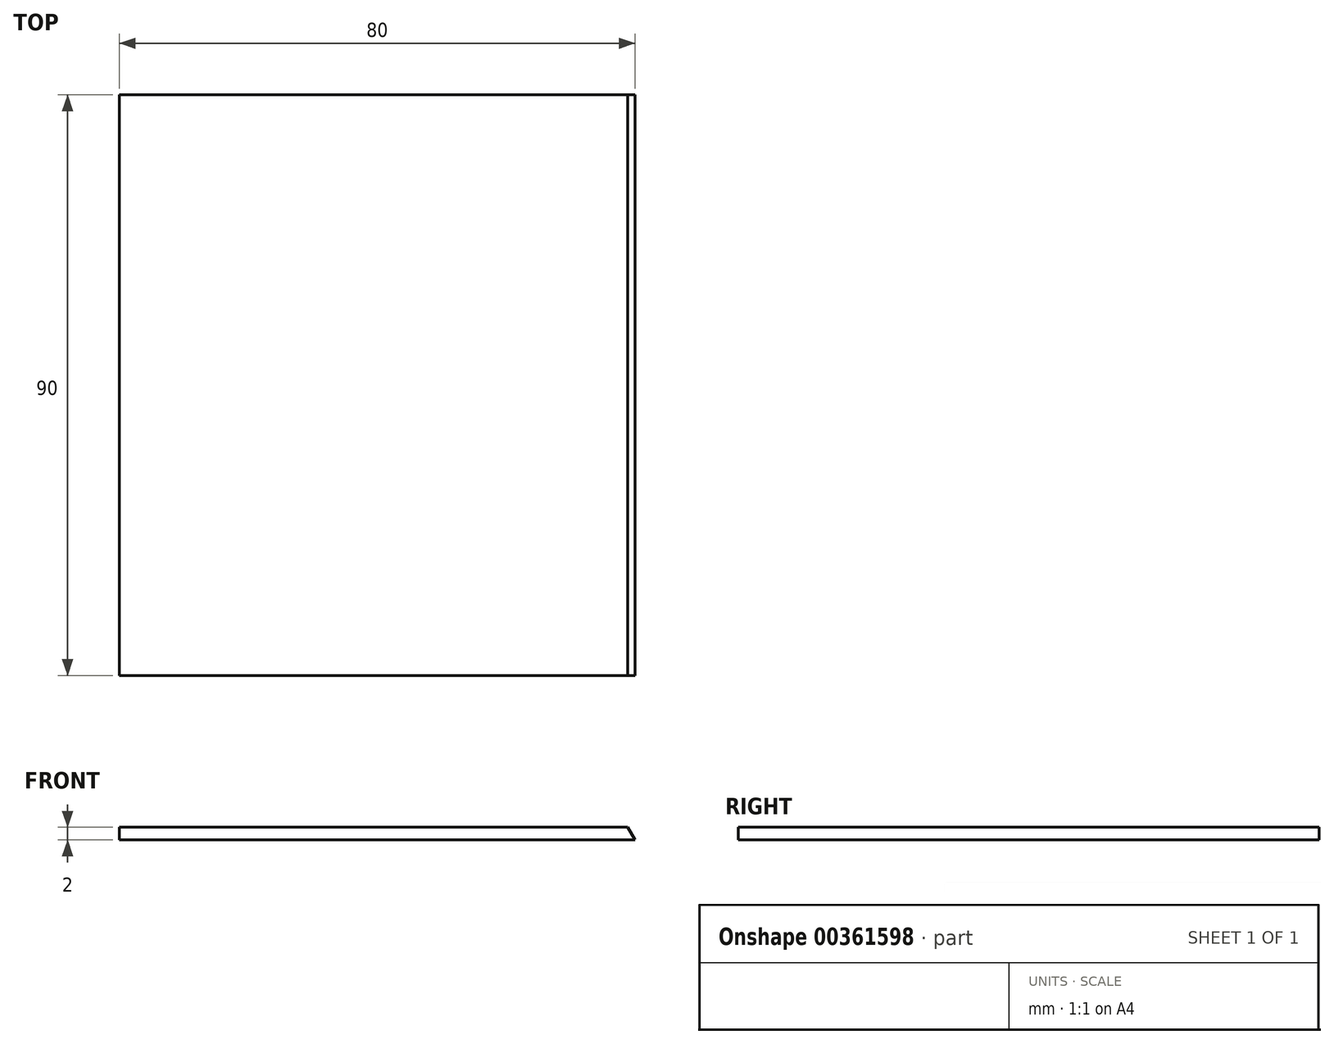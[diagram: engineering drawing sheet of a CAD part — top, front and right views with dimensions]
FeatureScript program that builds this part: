
annotation { "Feature Type Name" : "Feature", "Feature Type Description" : "" }
export const myFeature = defineFeature(function(context is Context, id is Id, definition is map)
    precondition{}
    {
        {
            var Q0;
            Q0=qCreatedBy(makeId("Front.planeOp"),FACE);
            var sketch = newSketch(context, id + "F0", { "sketchPlane" : qUnion([Q0])});
            skLineSegment(sketch, "E0", {"start": v(0, 0) * mm, "end": v(-1.15, 2) * mm});
            skLineSegment(sketch, "E1", {"start": v(-1.15, 2) * mm, "end": v(-80, 2) * mm});
            skLineSegment(sketch, "E2", {"start": v(-80, 2) * mm, "end": v(-80, 0) * mm});
            skLineSegment(sketch, "E3", {"start": v(-80, 0) * mm, "end": v(0, 0) * mm});
            skSolve(sketch);
        }
        {
            var Q0;
            Q0=makeQuery(id+"F0.imprint","IMPRINT",FACE,{"disambiguationData":[TD([[makeQuery(id+"F0.imprint","IMPRINT",EDGE,{"derivedFrom":sQuery(id+"F0.wireOp",EDGE,"E0")}),1.0]])]});
            extrude(context, id + "F1", {"entities" : qUnion([Q0]), "endBound" : BoundingType.SYMMETRIC, "depth" : 90 * mm});
        }
    });
